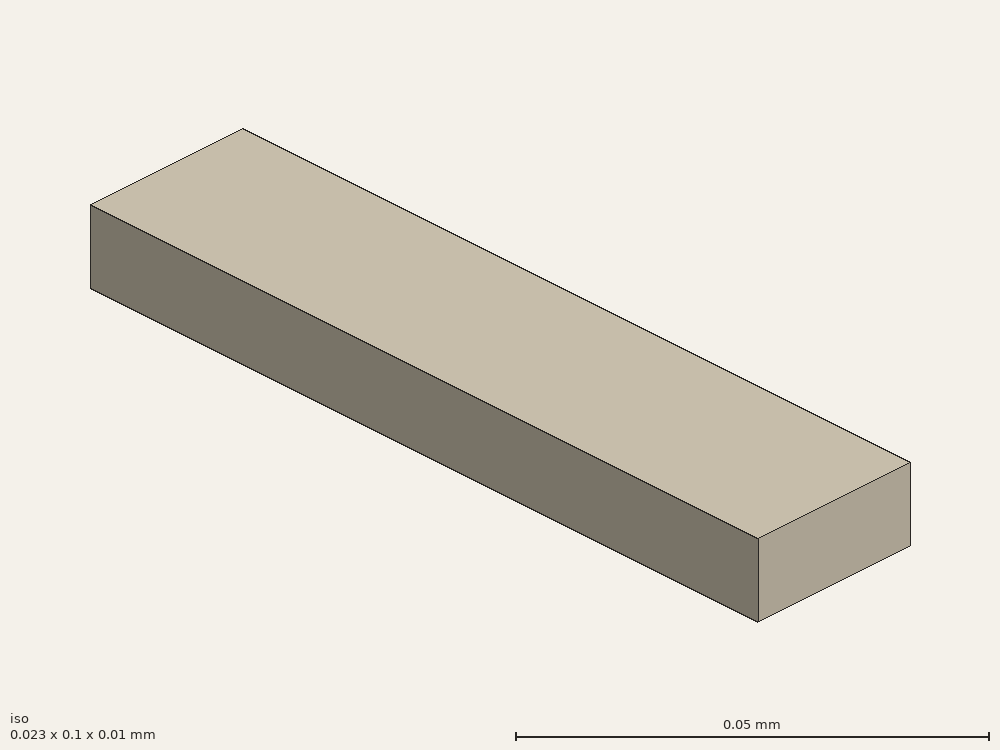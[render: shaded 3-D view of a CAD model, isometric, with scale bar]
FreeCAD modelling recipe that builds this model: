
FCSTD DOCUMENT  (FreeCAD 0.21R33694 (Git))
Label: straight-rotated
License: All rights reserved
LicenseURL: http://en.wikipedia.org/wiki/All_rights_reserved
objects: Part::Part2DObjectPython×5, App::FeaturePython×4, Part::Extrusion×1, Part::FeaturePython×1
note: 7 computed .brp shape members not serialized (recipe doc carries the construction recipe); baked Part::Feature solids carry a one-line shape summary decoded from their .brp

FEATURE [Part::Part2DObjectPython] Rectangle  # Draft 2D object (typed FeaturePython)
  Area = 232.258
  ChamferSize = 0
  Columns = 1
  FilletRadius = 0
  Height = 10.16
  Length = 22.86
  MakeFace = true
  Placement = pos=(-11.43,-5.08,0) rot=(0,0,1;0rad)
  Rows = 1
FEATURE [Part::Extrusion] Extrude
  Base = -> Rectangle
  Dir = (0,0,1)
  DirMode = 2
  FaceMakerClass = Part::FaceMakerBullseye
  LengthFwd = 100
  LengthRev = 0
  Solid = false
  Symmetric = false
FEATURE [Part::FeaturePython] Clone  label="Extrude001"  # Draft clone (typed FeaturePython)
  AttacherType = Attacher::AttachEngine3D
  Fuse = false
  Objects = -> [Extrude]
  Placement = pos=(0,0,0) rot=(1,0,0;1.5708rad)
  Scale = (0.001,0.001,0.001)
FEATURE [Part::Part2DObjectPython] Rectangle001  label="_Pport1"  # Draft 2D object (typed FeaturePython)
  Area = 0.000232258
  ChamferSize = 0
  Columns = 1
  FilletRadius = 0
  Height = 0.01016
  Length = 0.02286
  MakeFace = true
  Placement = pos=(-0.01143,-0.1,-0.00508) rot=(1,0,0;1.5708rad)
  Rows = 1
FEATURE [Part::Part2DObjectPython] Line  label="_Pv1"  # Draft 2D object (typed FeaturePython)
  Area = 0
  ChamferSize = 0
  Closed = false
  End = (-1.8e-15,-0.1,0.00508)
  FilletRadius = 0
  Length = 0.01016
  MakeFace = true
  Placement = pos=(0,-0.1,-0.00508) rot=(1,0,0;1.5708rad)
  Points = (2) [(0,0,0),(-1.77605e-15,0.01016,0)]
  Start = (0,-0.1,-0.00508)
  Subdivisions = 0
FEATURE [Part::Part2DObjectPython] Rectangle002  label="_Pport2"  # Draft 2D object (typed FeaturePython)
  Area = 0.000232258
  ChamferSize = 0
  Columns = 1
  FilletRadius = 0
  Height = 0.01016
  Length = 0.02286
  MakeFace = true
  Placement = pos=(-0.01143,0,-0.00508) rot=(1,0,0;1.5708rad)
  Rows = 1
FEATURE [Part::Part2DObjectPython] Line001  label="_Pv2"  # Draft 2D object (typed FeaturePython)
  Area = 0
  ChamferSize = 0
  Closed = false
  End = (0,0,0.00508)
  FilletRadius = 0
  Length = 0.01016
  MakeFace = true
  Placement = pos=(0,0,-0.00508) rot=(1,0,0;1.5708rad)
  Points = (2) [(0,0,0),(3.1106e-19,0.01016,0)]
  Start = (0,0,-0.00508)
  Subdivisions = 0
FEATURE [App::FeaturePython] Text  label="_S1(PV){port1}"  # WARN: FeaturePython — macro-defined, semantics opaque (R4)
  Placement = pos=(0.0413747,-0.017509,0) rot=(0,0,1;0rad)
  Text = .
FEATURE [App::FeaturePython] Text001  label="_S2(PV){port2}"  # WARN: FeaturePython — macro-defined, semantics opaque (R4)
  Placement = pos=(0.0413747,-0.017509,0) rot=(0,0,1;0rad)
  Text = .
FEATURE [App::FeaturePython] Text002  label="_L1(1,voltage){v1}"  # WARN: FeaturePython — macro-defined, semantics opaque (R4)
  Placement = pos=(0.0413747,-0.017509,0) rot=(0,0,1;0rad)
  Text = .
FEATURE [App::FeaturePython] Text003  label="_L2(2,voltage){v2}"  # WARN: FeaturePython — macro-defined, semantics opaque (R4)
  Placement = pos=(0.0413747,-0.017509,0) rot=(0,0,1;0rad)
  Text = .
